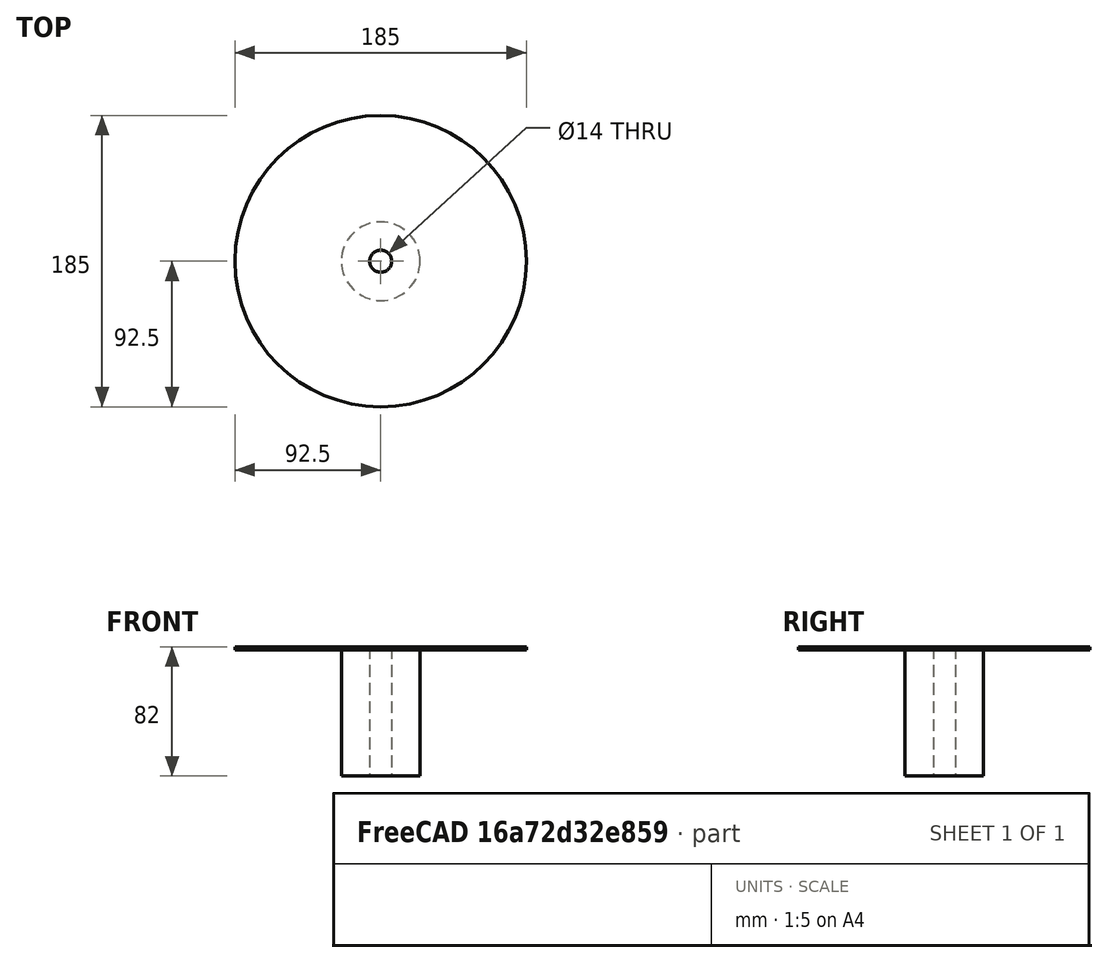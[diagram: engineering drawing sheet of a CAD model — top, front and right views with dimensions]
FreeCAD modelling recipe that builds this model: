
FCSTD DOCUMENT  (FreeCAD 0.19R24291 (Git))
Label: PVC
License: All rights reserved
LicenseURL: http://en.wikipedia.org/wiki/All_rights_reserved
objects: Sketcher::SketchObject×2, PartDesign::Revolution×1, PartDesign::Hole×1, PartDesign::Body×1
note: 7 computed .brp shape members not serialized (recipe doc carries the construction recipe); baked Part::Feature solids carry a one-line shape summary decoded from their .brp

FEATURE [Sketcher::SketchObject] Sketch
  FullyConstrained = true
  MapMode = 5
  Placement = pos=(0,0,0) rot=(1,0,0;1.5708rad)
  Support = -> [XZ_Plane]
  sketch-geometry (10):
    g0: LineSegment StartX=0 StartY=5.6986e-12 StartZ=0 EndX=-25 EndY=5.6986e-12 EndZ=0
    g1: LineSegment StartX=-25 StartY=5.6986e-12 StartZ=0 EndX=-25 EndY=40 EndZ=0
    g2: LineSegment StartX=-25 StartY=40 StartZ=0 EndX=-19 EndY=40 EndZ=0
    g3: LineSegment StartX=-19 StartY=40 StartZ=0 EndX=-19 EndY=40 EndZ=0
    g4: LineSegment StartX=-19 StartY=40 StartZ=0 EndX=-25 EndY=40 EndZ=0
    g5: LineSegment StartX=-25 StartY=40 StartZ=0 EndX=-25 EndY=80 EndZ=0
    g6: LineSegment StartX=-25 StartY=80 StartZ=0 EndX=-92.5 EndY=80 EndZ=0
    g7: LineSegment StartX=-92.5 StartY=80 StartZ=0 EndX=-92.5 EndY=82 EndZ=0
    g8: LineSegment StartX=-92.5 StartY=82 StartZ=0 EndX=0 EndY=82 EndZ=0
    g9: LineSegment StartX=0 StartY=82 StartZ=0 EndX=0 EndY=5.6986e-12 EndZ=0
  constraints (29):
    c: Coincident(g0,g-1)
    c: Horizontal(g0)
    c: Coincident(g1,g0)
    c: Vertical(g1)
    c: Coincident(g2,g1)
    c: Horizontal(g2)
    c: Coincident(g3,g2)
    c: Vertical(g3)
    c: DistanceX(g0,g0) = 25
    c: DistanceY(g1,g1) = 40
    c: DistanceY(g3,g3) = 0
    c: Coincident(g4,g3)
    c: Horizontal(g4)
    c: DistanceX(g2,g2) = 6
    c: DistanceX(g4,g4) = 6
    c: Coincident(g5,g4)
    c: Vertical(g5)
    c: Coincident(g6,g5)
    c: Horizontal(g6)
    c: DistanceY(g5,g5) = 40
    c: DistanceX(g6,g6) = 67.5
    c: Coincident(g7,g6)
    c: Vertical(g7)
    c: DistanceY(g7,g7) = 2
    c: Coincident(g8,g7)
    c: PointOnObject(g8,g-2)
    c: Horizontal(g8)
    c: Coincident(g9,g8)
    c: Coincident(g9,g0)
FEATURE [PartDesign::Revolution] Revolution
  Angle = 360
  Axis = (0,-2e-16,1)
  Base = (0,0,0)
  Placement = pos=(0,0,0) rot=(1,0,0;1.5708rad)
  Profile = -> Sketch
  ReferenceAxis = -> Sketch [V_Axis]
FEATURE [Sketcher::SketchObject] Sketch001
  FullyConstrained = true
  MapMode = 5
  Placement = pos=(0,-1.82e-14,82) rot=(0,0,1;3.14159rad)
  Support = -> [Revolution]
  sketch-geometry (1):
    g0: Circle CenterX=0 CenterY=0 CenterZ=0 NormalX=0 NormalY=0 NormalZ=1 AngleXU=0 Radius=7
  constraints (2):
    c: Coincident(g0,g-1)
    c: Diameter(g0) = 14
FEATURE [PartDesign::Hole] Hole
  BaseFeature = -> Revolution
  Depth = 25
  DepthType = 1
  Diameter = 14
  DrillForDepth = false
  DrillPoint = 1
  DrillPointAngle = 118
  HoleCutCountersinkAngle = 90
  HoleCutCustomValues = false
  HoleCutDepth = 0
  HoleCutDiameter = 6.1
  HoleCutType = 0
  ModelActualThread = false
  Placement = pos=(0,0,0) rot=(1,0,0;1.5708rad)
  Profile = -> Sketch001
  Tapered = false
  TaperedAngle = 90
  ThreadAngle = 0
  ThreadClass = 0
  ThreadCutOffInner = 0
  ThreadCutOffOuter = 0
  ThreadDirection = 0
  ThreadFit = 0
  ThreadPitch = 0
  ThreadSize = 0
  ThreadType = 0
  Threaded = false
FEATURE [PartDesign::Body] Body
  Group = -> [Sketch,Revolution,Sketch001,Hole]
  Origin = -> Origin
  Tip = -> Hole
